# Revit family: Faucet_Riser-Floor_Mount-KOHLER-FINIAL-K-607T
name_source: partatom
category: Plumbing Fixtures
revit_build: Autodesk Revit 2017 (Build: 20160225_1515(x64)
units: mm (PartAtom-declared; Revit-internal decimal feet)

## family parameters
Cut with Voids When Loaded = No
Host = Face
OmniClass Number = 23.31.11.00
OmniClass Title = Faucets
Part Type = Normal
Room Calculation Point = No
Round Connector Dimension = Use Diameter
Shared = No

## types (5) — shared parameters
ADA Compliant = No
Assembly Code = D2010
CW Connection = Yes
Cold Water Inlet = Cold Water Inlet
Date Modified = 12/09/2020
Default Elevation = 0"
Description = Floor Stand 80cm
Drain Included = No
Faucet Hole Spacing = 0"
Flow Rate = 0 GPM
HW Connection = Yes
Handle Clearance = 0"
Height = 29 5/16"
Hot Water Inlet = Hot Water Inlet
Length = 4 15/16"
Manufacturer = KOHLER Co.
Master Format 2014 = 22 41 39
Master Format 2014 Name = Residential Faucets, Supplies, and Trim
Material = Premium metal Construction
Pressure = 0.00 psi
Product Documentation Link = https://files.kohler.com.cn
Product Name = FINIAL
Product Page URL = https://www.kohler.com.cn
Spout Reach = 0"
URL = http://www.kohler.com.cn
Vent Connection = No
Waste Connection = No
Waste Water Outlet = Waste Water Outlet
WaterSense Certified = No
Width = 10 1/4"

## per-type parameters (varying)
| type | Finish | Model | Type |
| CP- Polished Chrome | Kohler-Metal-CP-Polished_Chrome | K-607T-CP | 1 |
| AF- Flange Gold | Kohler-Metal-AF-Flange_Gold | K-607T-AF | 2 |
| SN- Champagne Gold | Kohler-Metal-SN-Champagne_Gold | K-607T-SN | 3 |
| BN- Roman Silver | Kohler-Metal-BN-Roman_Silver | K-607T-BN | 4 |
| R2B- Black Yaojin | Kohler-Metal-R2B-Black_Yaojin | K-607T-R2B | 5 |

## geometry (parser evidence)
native form markers: Sweep x5
no freeform markers — native parametric forms only
